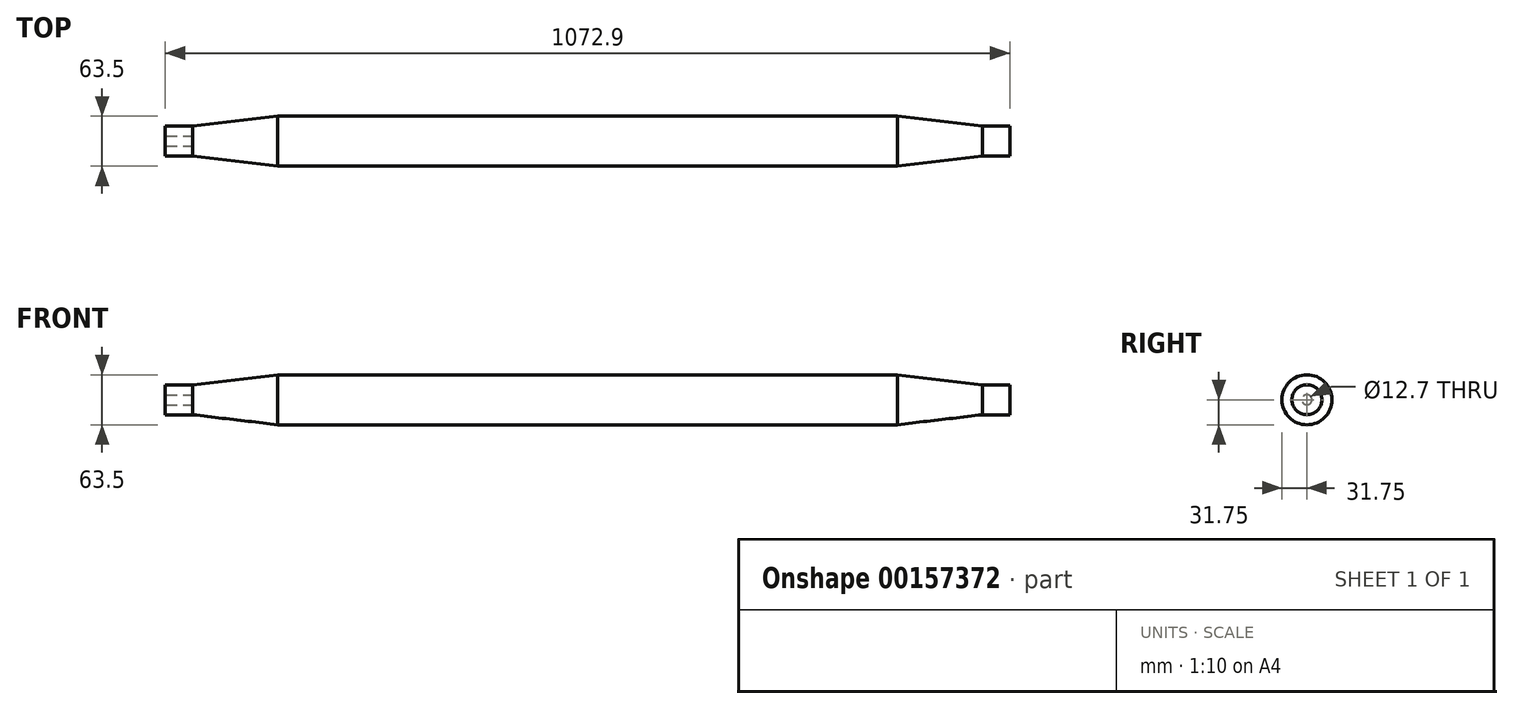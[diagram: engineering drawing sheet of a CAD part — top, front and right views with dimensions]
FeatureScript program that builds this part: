
annotation { "Feature Type Name" : "Feature", "Feature Type Description" : "" }
export const myFeature = defineFeature(function(context is Context, id is Id, definition is map)
    precondition{}
    {
        {
            var Q0;
            Q0=qCreatedBy(makeId("Right.planeOp"),FACE);
            var sketch = newSketch(context, id + "F0", { "sketchPlane" : qUnion([Q0])});
            skCircle(sketch, "E0", {"center": v(0, 0) * mm, "radius": 31.75 * mm});
            skSolve(sketch);
        }
        {
            var Q0;
            Q0=qSketchRegion(id+"F0",true);
            extrude(context, id + "F1", {"entities" : qUnion([Q0]), "endBound" : BoundingType.SYMMETRIC, "depth" : 787.4 * mm});
        }
        {
            var Q0;
            Q0=makeQuery(id+"F1.opExtrude","CAP_FACE",FACE,{"disambiguationData":[OSD([sQuery(id+"F0.wireOp",EDGE,"E0")])],"isStart":false});
            cPlane(context, id + "F2", {"entities" : qUnion([Q0]), "cplaneType" : CPlaneType.OFFSET, "offset" : 142.75 * mm, "width" : 152.4 * mm, "height" : 152.4 * mm});
        }
        {
            var Q0;
            Q0=qCreatedBy(id+"F2.planeOp",FACE);
            var sketch = newSketch(context, id + "F3", { "sketchPlane" : qUnion([Q0])});
            skCircle(sketch, "E1", {"center": v(0, 0) * mm, "radius": 19.05 * mm});
            skSolve(sketch);
        }
        {
            var Q0;
            Q0=qSketchRegion(id+"F3",true);
            extrude(context, id + "F4", {"entities" : qUnion([Q0]), "oppositeDirection" : true, "depth" : 35.05 * mm});
        }
        {
            var Q0;
            Q0=makeQuery(id+"F4.opExtrude","SWEPT_BODY",BODY,{"disambiguationData":[OSD([sQuery(id+"F3.wireOp",EDGE,"E1")])]});
            var Q1;
            Q1=qCreatedBy(makeId("Right.planeOp"),FACE);
            mirror(context, id + "F5", {"entities" : qUnion([Q0]), "mirrorPlane" : qUnion([Q1])});
        }
        {
            var Q0;
            Q0=makeQuery(id+"F1.opExtrude","CAP_FACE",FACE,{"disambiguationData":[OSD([sQuery(id+"F0.wireOp",EDGE,"E0")])],"isStart":false});
            var Q1;
            Q1=makeQuery(id+"F4.opExtrude","CAP_FACE",FACE,{"disambiguationData":[OSD([sQuery(id+"F3.wireOp",EDGE,"E1")])],"isStart":false});
            loft(context, id + "F6", {"sheetProfilesArray" : [{ "sheetProfileEntities" : qUnion([Q0]) }, { "sheetProfileEntities" : qUnion([Q1]) }]});
        }
        {
            var Q0;
            Q0=makeQuery(id+"F1.opExtrude","CAP_FACE",FACE,{"disambiguationData":[OSD([sQuery(id+"F0.wireOp",EDGE,"E0")])],"isStart":true});
            var Q1;
            Q1=makeQuery(id+"F5.opPattern","COPY",FACE,{"derivedFrom":makeQuery(id+"F4.opExtrude","CAP_FACE",FACE,{"disambiguationData":[OSD([sQuery(id+"F3.wireOp",EDGE,"E1")])],"isStart":false}),"instanceName":"1"});
            loft(context, id + "F7", {"sheetProfilesArray" : [{ "sheetProfileEntities" : qUnion([Q0]) }, { "sheetProfileEntities" : qUnion([Q1]) }]});
        }
        {
            var Q0;
            Q0=qCreatedBy(id+"F2.planeOp",FACE);
            var sketch = newSketch(context, id + "F8", { "sketchPlane" : qUnion([Q0])});
            skPoint(sketch, "E2", {"position": v(0, 0) * mm});
            skSolve(sketch);
        }
        {
            var Q0;
            Q0=sQuery(id+"F8.wireOp",VERTEX,"E2");
            var Q1;
            Q1=makeQuery(id+"F5.opPattern","COPY",BODY,{"derivedFrom":makeQuery(id+"F4.opExtrude","SWEPT_BODY",BODY,{"disambiguationData":[OSD([sQuery(id+"F3.wireOp",EDGE,"E1")])]}),"instanceName":"1"});
            hole(context, id + "F9", {"style" : HoleStyle.SIMPLE, "holeDiameter" : 12.7 * mm, "endStyle" : HoleEndStyle.BLIND, "holeDepth" : 44.45 * mm, "locations" : qUnion([Q0]), "scope" : qUnion([Q1])});
        }
        {
            var Q0;
            Q0=makeQuery(id+"F5.opPattern","COPY",FACE,{"derivedFrom":makeQuery(id+"F4.opExtrude","CAP_FACE",FACE,{"disambiguationData":[OSD([sQuery(id+"F3.wireOp",EDGE,"E1")])],"isStart":true}),"instanceName":"1"});
            var sketch = newSketch(context, id + "F10", { "sketchPlane" : qUnion([Q0])});
            skPoint(sketch, "E3", {"position": v(0, 0) * mm});
            skSolve(sketch);
        }
        {
            var Q0;
            Q0=sQuery(id+"F10.wireOp",VERTEX,"E3");
            var Q1;
            Q1=makeQuery(id+"F5.opPattern","COPY",BODY,{"derivedFrom":makeQuery(id+"F4.opExtrude","SWEPT_BODY",BODY,{"disambiguationData":[OSD([sQuery(id+"F3.wireOp",EDGE,"E1")])]}),"instanceName":"1"});
            hole(context, id + "F11", {"style" : HoleStyle.SIMPLE, "holeDiameter" : 12.7 * mm, "endStyle" : HoleEndStyle.BLIND, "holeDepth" : 44.45 * mm, "locations" : qUnion([Q0]), "scope" : qUnion([Q1])});
        }
    });
